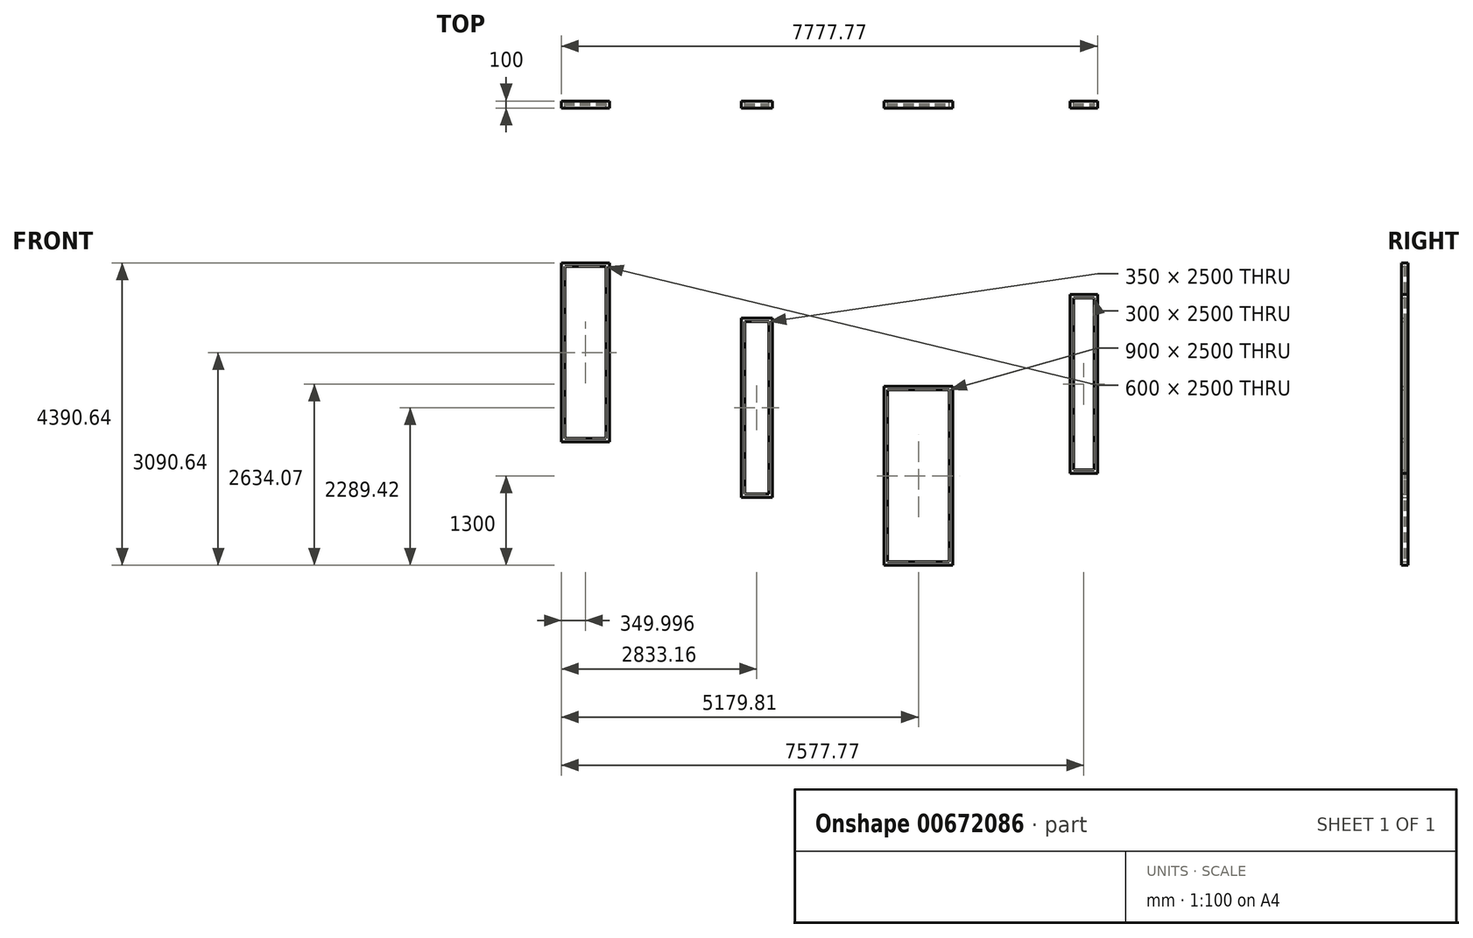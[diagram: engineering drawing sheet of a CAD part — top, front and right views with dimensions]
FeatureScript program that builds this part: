
annotation { "Feature Type Name" : "Feature", "Feature Type Description" : "" }
export const myFeature = defineFeature(function(context is Context, id is Id, definition is map)
    precondition{}
    {
        {
            var Q0;
            Q0=qCreatedBy(makeId("Front.planeOp"),FACE);
            var sketch = newSketch(context, id + "F0", { "sketchPlane" : qUnion([Q0])});
            skLineSegment(sketch, "E0.bottom", {"start": v(-234.89, 2206.93) * mm, "end": v(215.11, 2206.93) * mm});
            skLineSegment(sketch, "E0.top", {"start": v(-234.89, -393.07) * mm, "end": v(215.11, -393.07) * mm});
            skLineSegment(sketch, "E0.left", {"start": v(-234.89, 2206.93) * mm, "end": v(-234.89, -393.07) * mm});
            skLineSegment(sketch, "E0.right", {"start": v(215.11, 2206.93) * mm, "end": v(215.11, -393.07) * mm});
            skLineSegment(sketch, "E1.0", {"start": v(-184.89, 2156.93) * mm, "end": v(165.11, 2156.93) * mm});
            skLineSegment(sketch, "E1.1", {"start": v(-184.89, 2156.93) * mm, "end": v(-184.89, -343.07) * mm});
            skLineSegment(sketch, "E1.2", {"start": v(-184.89, -343.07) * mm, "end": v(165.11, -343.07) * mm});
            skLineSegment(sketch, "E1.3", {"start": v(165.11, 2156.93) * mm, "end": v(165.11, -343.07) * mm});
            skSolve(sketch);
        }
        {
            var Q0;
            Q0 = qSketchRegion(id + "F0", true);
            extrude(context, id + "F1", {"entities" : qUnion([Q0]), "depth" : 100 * mm, "offsetDistance" : 25 * mm});
        }
        {
            var Q0;
            Q0=makeQuery(id+"F1.opExtrude","CAP_FACE",FACE,{"disambiguationData":[OSD([sQuery(id+"F0.wireOp",EDGE,"E0.bottom"),sQuery(id+"F0.wireOp",EDGE,"E0.top"),sQuery(id+"F0.wireOp",EDGE,"E0.left"),sQuery(id+"F0.wireOp",EDGE,"E0.right"),sQuery(id+"F0.wireOp",EDGE,"E1.0"),sQuery(id+"F0.wireOp",EDGE,"E1.1"),sQuery(id+"F0.wireOp",EDGE,"E1.2"),sQuery(id+"F0.wireOp",EDGE,"E1.3")])],"isStart":false});
            var Q1;
            Q1=makeQuery(id+"F1.opExtrude","CAP_FACE",FACE,{"disambiguationData":[OSD([sQuery(id+"F0.wireOp",EDGE,"E0.bottom"),sQuery(id+"F0.wireOp",EDGE,"E0.top"),sQuery(id+"F0.wireOp",EDGE,"E0.left"),sQuery(id+"F0.wireOp",EDGE,"E0.right"),sQuery(id+"F0.wireOp",EDGE,"E1.0"),sQuery(id+"F0.wireOp",EDGE,"E1.1"),sQuery(id+"F0.wireOp",EDGE,"E1.2"),sQuery(id+"F0.wireOp",EDGE,"E1.3")])],"isStart":true});
            cPlane(context, id + "F2", {"entities" : qUnion([Q0, Q1]), "cplaneType" : CPlaneType.MID_PLANE, "offset" : 25 * mm, "width" : 150 * mm, "height" : 150 * mm});
        }
        {
            var Q0;
            Q0=qCreatedBy(id+"F2.planeOp",FACE);
            var sketch = newSketch(context, id + "F3", { "sketchPlane" : qUnion([Q0])});
            skLineSegment(sketch, "E2.0", {"start": v(-184.89, -343.07) * mm, "end": v(165.11, -343.07) * mm});
            skLineSegment(sketch, "E2.1", {"start": v(-184.89, 2156.93) * mm, "end": v(-184.89, -343.07) * mm});
            skLineSegment(sketch, "E2.2", {"start": v(165.11, 2156.93) * mm, "end": v(165.11, -343.07) * mm});
            skLineSegment(sketch, "E2.3", {"start": v(-184.89, 2156.93) * mm, "end": v(165.11, 2156.93) * mm});
            skSolve(sketch);
        }
        {
            var Q0;
            Q0 = qSketchRegion(id + "F3", true);
            extrude(context, id + "F4", {"entities" : qUnion([Q0]), "endBound" : BoundingType.SYMMETRIC, "depth" : 25 * mm, "offsetDistance" : 25 * mm});
        }
        {
            var Q0;
            Q0=qCreatedBy(makeId("Front.planeOp"),FACE);
            var sketch = newSketch(context, id + "F5", { "sketchPlane" : qUnion([Q0])});
            skLineSegment(sketch, "E3.bottom", {"start": v(-2143.04, 3008.15) * mm, "end": v(-2843.04, 3008.15) * mm});
            skLineSegment(sketch, "E3.top", {"start": v(-2143.04, 408.15) * mm, "end": v(-2843.04, 408.15) * mm});
            skLineSegment(sketch, "E3.left", {"start": v(-2143.04, 3008.15) * mm, "end": v(-2143.04, 408.15) * mm});
            skLineSegment(sketch, "E3.right", {"start": v(-2843.04, 3008.15) * mm, "end": v(-2843.04, 408.15) * mm});
            skLineSegment(sketch, "E4.0", {"start": v(-2193.04, 2958.15) * mm, "end": v(-2793.04, 2958.15) * mm});
            skLineSegment(sketch, "E4.1", {"start": v(-2193.04, 2958.15) * mm, "end": v(-2193.04, 458.15) * mm});
            skLineSegment(sketch, "E4.2", {"start": v(-2193.04, 458.15) * mm, "end": v(-2793.04, 458.15) * mm});
            skLineSegment(sketch, "E4.3", {"start": v(-2793.04, 2958.15) * mm, "end": v(-2793.04, 458.15) * mm});
            skSolve(sketch);
        }
        {
            var Q0;
            Q0 = qSketchRegion(id + "F5", true);
            extrude(context, id + "F6", {"entities" : qUnion([Q0]), "depth" : 100 * mm, "offsetDistance" : 25 * mm});
        }
        {
            var Q0;
            Q0=makeQuery(id+"F6.opExtrude","CAP_FACE",FACE,{"disambiguationData":[OSD([sQuery(id+"F5.wireOp",EDGE,"E3.bottom"),sQuery(id+"F5.wireOp",EDGE,"E3.top"),sQuery(id+"F5.wireOp",EDGE,"E3.left"),sQuery(id+"F5.wireOp",EDGE,"E3.right"),sQuery(id+"F5.wireOp",EDGE,"E4.0"),sQuery(id+"F5.wireOp",EDGE,"E4.1"),sQuery(id+"F5.wireOp",EDGE,"E4.2"),sQuery(id+"F5.wireOp",EDGE,"E4.3")])],"isStart":true});
            var Q1;
            Q1=makeQuery(id+"F6.opExtrude","CAP_FACE",FACE,{"disambiguationData":[OSD([sQuery(id+"F5.wireOp",EDGE,"E3.bottom"),sQuery(id+"F5.wireOp",EDGE,"E3.top"),sQuery(id+"F5.wireOp",EDGE,"E3.left"),sQuery(id+"F5.wireOp",EDGE,"E3.right"),sQuery(id+"F5.wireOp",EDGE,"E4.0"),sQuery(id+"F5.wireOp",EDGE,"E4.1"),sQuery(id+"F5.wireOp",EDGE,"E4.2"),sQuery(id+"F5.wireOp",EDGE,"E4.3")])],"isStart":false});
            cPlane(context, id + "F7", {"entities" : qUnion([Q0, Q1]), "cplaneType" : CPlaneType.MID_PLANE, "offset" : 25 * mm, "width" : 150 * mm, "height" : 150 * mm});
        }
        {
            var Q0;
            Q0=qCreatedBy(id+"F7.planeOp",FACE);
            var sketch = newSketch(context, id + "F8", { "sketchPlane" : qUnion([Q0])});
            skLineSegment(sketch, "E5.0", {"start": v(2193.04, 2958.15) * mm, "end": v(2793.04, 2958.15) * mm});
            skLineSegment(sketch, "E5.1", {"start": v(2793.04, 2958.15) * mm, "end": v(2793.04, 458.15) * mm});
            skLineSegment(sketch, "E5.2", {"start": v(2193.04, 2958.15) * mm, "end": v(2193.04, 458.15) * mm});
            skLineSegment(sketch, "E5.3", {"start": v(2193.04, 458.15) * mm, "end": v(2793.04, 458.15) * mm});
            skSolve(sketch);
        }
        {
            var Q0;
            Q0 = qSketchRegion(id + "F8", true);
            extrude(context, id + "F9", {"entities" : qUnion([Q0]), "endBound" : BoundingType.SYMMETRIC, "depth" : 25 * mm, "offsetDistance" : 25 * mm});
        }
        {
            var Q0;
            Q0=qCreatedBy(makeId("Front.planeOp"),FACE);
            var sketch = newSketch(context, id + "F10", { "sketchPlane" : qUnion([Q0])});
            skLineSegment(sketch, "E6.bottom", {"start": v(4534.73, 2551.57) * mm, "end": v(4934.73, 2551.57) * mm});
            skLineSegment(sketch, "E6.top", {"start": v(4534.73, -48.43) * mm, "end": v(4934.73, -48.43) * mm});
            skLineSegment(sketch, "E6.left", {"start": v(4534.73, 2551.57) * mm, "end": v(4534.73, -48.43) * mm});
            skLineSegment(sketch, "E6.right", {"start": v(4934.73, 2551.57) * mm, "end": v(4934.73, -48.43) * mm});
            skLineSegment(sketch, "E7.0", {"start": v(4584.73, 2501.57) * mm, "end": v(4884.73, 2501.57) * mm});
            skLineSegment(sketch, "E7.1", {"start": v(4584.73, 2501.57) * mm, "end": v(4584.73, 1.57) * mm});
            skLineSegment(sketch, "E7.2", {"start": v(4584.73, 1.57) * mm, "end": v(4884.73, 1.57) * mm});
            skLineSegment(sketch, "E7.3", {"start": v(4884.73, 2501.57) * mm, "end": v(4884.73, 1.57) * mm});
            skSolve(sketch);
        }
        {
            var Q0;
            Q0 = qSketchRegion(id + "F10", true);
            extrude(context, id + "F11", {"entities" : qUnion([Q0]), "depth" : 100 * mm, "offsetDistance" : 25 * mm});
        }
        {
            var Q0;
            Q0=makeQuery(id+"F11.opExtrude","CAP_FACE",FACE,{"disambiguationData":[OSD([sQuery(id+"F10.wireOp",EDGE,"E6.bottom"),sQuery(id+"F10.wireOp",EDGE,"E6.top"),sQuery(id+"F10.wireOp",EDGE,"E6.left"),sQuery(id+"F10.wireOp",EDGE,"E6.right"),sQuery(id+"F10.wireOp",EDGE,"E7.0"),sQuery(id+"F10.wireOp",EDGE,"E7.1"),sQuery(id+"F10.wireOp",EDGE,"E7.2"),sQuery(id+"F10.wireOp",EDGE,"E7.3")])],"isStart":true});
            var Q1;
            Q1=makeQuery(id+"F11.opExtrude","CAP_FACE",FACE,{"disambiguationData":[OSD([sQuery(id+"F10.wireOp",EDGE,"E6.bottom"),sQuery(id+"F10.wireOp",EDGE,"E6.top"),sQuery(id+"F10.wireOp",EDGE,"E6.left"),sQuery(id+"F10.wireOp",EDGE,"E6.right"),sQuery(id+"F10.wireOp",EDGE,"E7.0"),sQuery(id+"F10.wireOp",EDGE,"E7.1"),sQuery(id+"F10.wireOp",EDGE,"E7.2"),sQuery(id+"F10.wireOp",EDGE,"E7.3")])],"isStart":false});
            cPlane(context, id + "F12", {"entities" : qUnion([Q0, Q1]), "cplaneType" : CPlaneType.MID_PLANE, "offset" : 25 * mm, "width" : 150 * mm, "height" : 150 * mm});
        }
        {
            var Q0;
            Q0=qCreatedBy(id+"F12.planeOp",FACE);
            var sketch = newSketch(context, id + "F13", { "sketchPlane" : qUnion([Q0])});
            skLineSegment(sketch, "E8.0", {"start": v(-4584.73, 2501.57) * mm, "end": v(-4884.73, 2501.57) * mm});
            skLineSegment(sketch, "E8.1", {"start": v(-4884.73, 2501.57) * mm, "end": v(-4884.73, 1.57) * mm});
            skLineSegment(sketch, "E8.2", {"start": v(-4584.73, 2501.57) * mm, "end": v(-4584.73, 1.57) * mm});
            skLineSegment(sketch, "E8.3", {"start": v(-4584.73, 1.57) * mm, "end": v(-4884.73, 1.57) * mm});
            skSolve(sketch);
        }
        {
            var Q0;
            Q0 = qSketchRegion(id + "F13", true);
            extrude(context, id + "F14", {"entities" : qUnion([Q0]), "endBound" : BoundingType.SYMMETRIC, "depth" : 25 * mm, "offsetDistance" : 25 * mm});
        }
        {
            var Q0;
            Q0=qCreatedBy(makeId("Front.planeOp"),FACE);
            var sketch = newSketch(context, id + "F15", { "sketchPlane" : qUnion([Q0])});
            skLineSegment(sketch, "E9.bottom", {"start": v(1836.77, 1217.5) * mm, "end": v(2836.77, 1217.5) * mm});
            skLineSegment(sketch, "E9.top", {"start": v(1836.77, -1382.5) * mm, "end": v(2836.77, -1382.5) * mm});
            skLineSegment(sketch, "E9.left", {"start": v(1836.77, 1217.5) * mm, "end": v(1836.77, -1382.5) * mm});
            skLineSegment(sketch, "E9.right", {"start": v(2836.77, 1217.5) * mm, "end": v(2836.77, -1382.5) * mm});
            skLineSegment(sketch, "E10.0", {"start": v(1886.77, 1167.5) * mm, "end": v(2786.77, 1167.5) * mm});
            skLineSegment(sketch, "E10.1", {"start": v(1886.77, 1167.5) * mm, "end": v(1886.77, -1332.5) * mm});
            skLineSegment(sketch, "E10.2", {"start": v(1886.77, -1332.5) * mm, "end": v(2786.77, -1332.5) * mm});
            skLineSegment(sketch, "E10.3", {"start": v(2786.77, 1167.5) * mm, "end": v(2786.77, -1332.5) * mm});
            skSolve(sketch);
        }
        {
            var Q0;
            Q0 = qSketchRegion(id + "F15", true);
            extrude(context, id + "F16", {"entities" : qUnion([Q0]), "depth" : 100 * mm, "offsetDistance" : 25 * mm});
        }
        {
            var Q0;
            Q0=makeQuery(id+"F16.opExtrude","CAP_FACE",FACE,{"disambiguationData":[OSD([sQuery(id+"F15.wireOp",EDGE,"E9.bottom"),sQuery(id+"F15.wireOp",EDGE,"E9.top"),sQuery(id+"F15.wireOp",EDGE,"E9.left"),sQuery(id+"F15.wireOp",EDGE,"E9.right"),sQuery(id+"F15.wireOp",EDGE,"E10.0"),sQuery(id+"F15.wireOp",EDGE,"E10.1"),sQuery(id+"F15.wireOp",EDGE,"E10.2"),sQuery(id+"F15.wireOp",EDGE,"E10.3")])],"isStart":false});
            var Q1;
            Q1=makeQuery(id+"F16.opExtrude","CAP_FACE",FACE,{"disambiguationData":[OSD([sQuery(id+"F15.wireOp",EDGE,"E9.bottom"),sQuery(id+"F15.wireOp",EDGE,"E9.top"),sQuery(id+"F15.wireOp",EDGE,"E9.left"),sQuery(id+"F15.wireOp",EDGE,"E9.right"),sQuery(id+"F15.wireOp",EDGE,"E10.0"),sQuery(id+"F15.wireOp",EDGE,"E10.1"),sQuery(id+"F15.wireOp",EDGE,"E10.2"),sQuery(id+"F15.wireOp",EDGE,"E10.3")])],"isStart":true});
            cPlane(context, id + "F17", {"entities" : qUnion([Q0, Q1]), "cplaneType" : CPlaneType.MID_PLANE, "offset" : 25 * mm, "width" : 150 * mm, "height" : 150 * mm});
        }
        {
            var Q0;
            Q0=qCreatedBy(id+"F17.planeOp",FACE);
            var sketch = newSketch(context, id + "F18", { "sketchPlane" : qUnion([Q0])});
            skLineSegment(sketch, "E11.0", {"start": v(1886.77, 1167.5) * mm, "end": v(2786.77, 1167.5) * mm});
            skLineSegment(sketch, "E11.1", {"start": v(2786.77, 1167.5) * mm, "end": v(2786.77, -1332.5) * mm});
            skLineSegment(sketch, "E11.2", {"start": v(1886.77, 1167.5) * mm, "end": v(1886.77, -1332.5) * mm});
            skLineSegment(sketch, "E11.3", {"start": v(1886.77, -1332.5) * mm, "end": v(2786.77, -1332.5) * mm});
            skSolve(sketch);
        }
        {
            var Q0;
            Q0 = qSketchRegion(id + "F18", true);
            extrude(context, id + "F19", {"entities" : qUnion([Q0]), "endBound" : BoundingType.SYMMETRIC, "depth" : 25 * mm, "offsetDistance" : 25 * mm});
        }
    });
